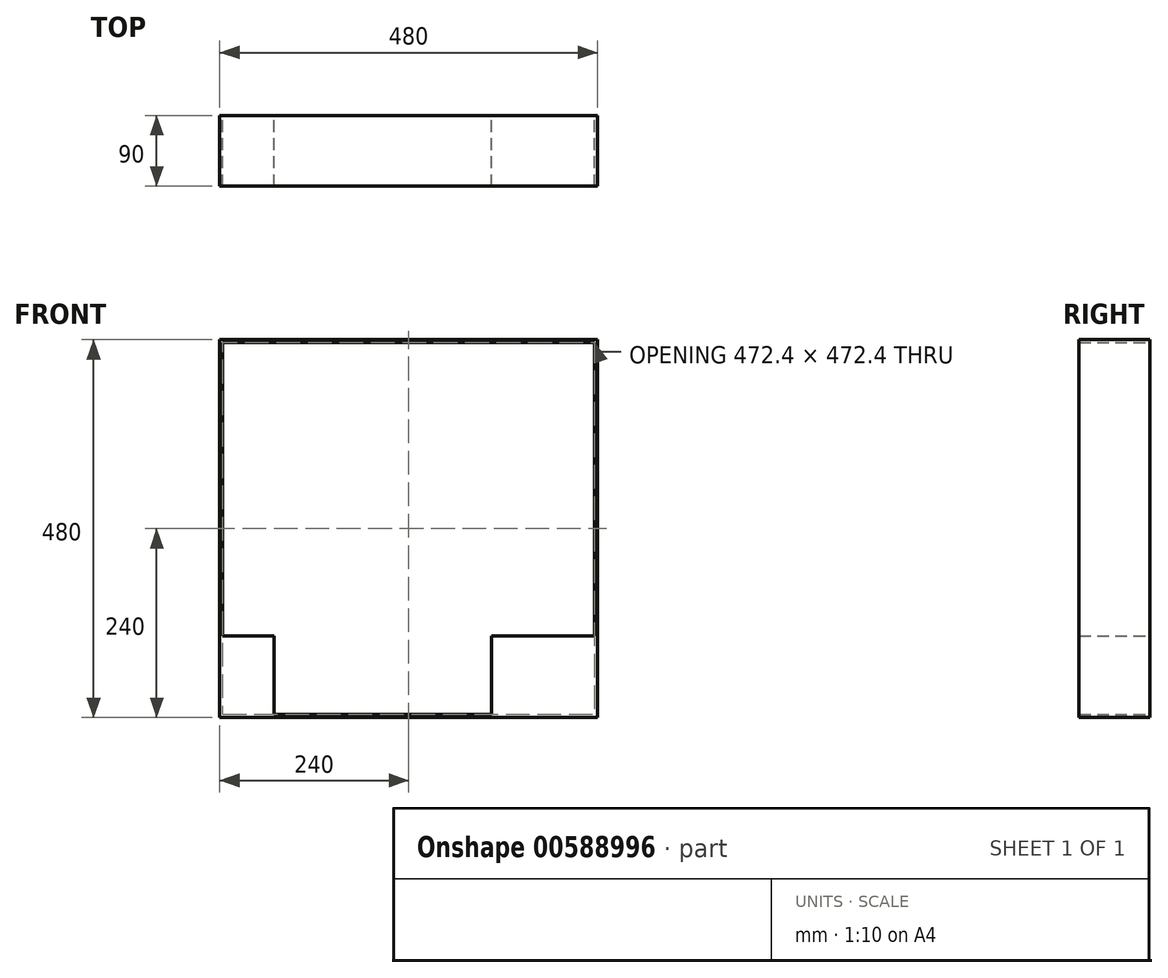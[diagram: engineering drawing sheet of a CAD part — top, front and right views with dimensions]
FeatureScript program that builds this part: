
annotation { "Feature Type Name" : "Feature", "Feature Type Description" : "" }
export const myFeature = defineFeature(function(context is Context, id is Id, definition is map)
    precondition{}
    {
        {
            var Q0;
            Q0=qCreatedBy(makeId("Front.planeOp"),FACE);
            var sketch = newSketch(context, id + "F0", { "sketchPlane" : qUnion([Q0])});
            skLineSegment(sketch, "E0.bottom", {"start": v(-240, -240) * mm, "end": v(240, -240) * mm});
            skLineSegment(sketch, "E0.top", {"start": v(-240, 240) * mm, "end": v(240, 240) * mm});
            skLineSegment(sketch, "E0.left", {"start": v(-240, -240) * mm, "end": v(-240, 240) * mm});
            skLineSegment(sketch, "E0.right", {"start": v(240, -240) * mm, "end": v(240, 240) * mm});
            skPoint(sketch, "E0.middle", {"position": v(0, 0) * mm});
            skLineSegment(sketch, "E1.bottom", {"start": v(-236.2, -236.2) * mm, "end": v(236.2, -236.2) * mm});
            skLineSegment(sketch, "E1.top", {"start": v(-236.2, 236.2) * mm, "end": v(236.2, 236.2) * mm});
            skLineSegment(sketch, "E1.left", {"start": v(-236.2, -236.2) * mm, "end": v(-236.2, 236.2) * mm});
            skLineSegment(sketch, "E1.right", {"start": v(236.2, -236.2) * mm, "end": v(236.2, 236.2) * mm});
            skLineSegment(sketch, "E2.bottom", {"start": v(-236.2, -136.2) * mm, "end": v(-170.8, -136.2) * mm});
            skLineSegment(sketch, "E2.top", {"start": v(-236.2, -236.2) * mm, "end": v(-170.8, -236.2) * mm});
            skLineSegment(sketch, "E2.left", {"start": v(-236.2, -136.2) * mm, "end": v(-236.2, -236.2) * mm});
            skLineSegment(sketch, "E2.right", {"start": v(-170.8, -136.2) * mm, "end": v(-170.8, -236.2) * mm});
            skLineSegment(sketch, "E3.bottom", {"start": v(236.2, -136.2) * mm, "end": v(105.4, -136.2) * mm});
            skLineSegment(sketch, "E3.top", {"start": v(236.2, -236.2) * mm, "end": v(105.4, -236.2) * mm});
            skLineSegment(sketch, "E3.left", {"start": v(236.2, -136.2) * mm, "end": v(236.2, -236.2) * mm});
            skLineSegment(sketch, "E3.right", {"start": v(105.4, -136.2) * mm, "end": v(105.4, -236.2) * mm});
            skPoint(sketch, "E4.middle", {"position": v(-9.3, 0) * mm});
            skSolve(sketch);
        }
        {
            var Q0;
            Q0=makeQuery(id+"F0.imprint","IMPRINT",FACE,{"disambiguationData":[TD([[makeQuery(id+"F0.imprint","IMPRINT",EDGE,{"derivedFrom":sQuery(id+"F0.wireOp",EDGE,"E0.bottom")}),1.0]])]});
            extrude(context, id + "F1", {"entities" : qUnion([Q0]), "depth" : 90 * mm, "offsetDistance" : 25 * mm});
        }
        {
            var Q0;
            Q0=makeQuery(id+"F0.imprint","IMPRINT",FACE,{"disambiguationData":[TD([[makeQuery(id+"F0.imprint","IMPRINT",EDGE,{"derivedFrom":sQuery(id+"F0.wireOp",EDGE,"E2.bottom")}),-1.0]])]});
            var Q1;
            Q1=makeQuery(id+"F0.imprint","IMPRINT",FACE,{"disambiguationData":[TD([[makeQuery(id+"F0.imprint","IMPRINT",EDGE,{"derivedFrom":sQuery(id+"F0.wireOp",EDGE,"E3.bottom")}),1.0]])]});
            extrude(context, id + "F2", {"entities" : qUnion([Q0, Q1]), "operationType" : NewBodyOperationType.ADD, "depth" : 90 * mm, "offsetDistance" : 25 * mm});
        }
    });
